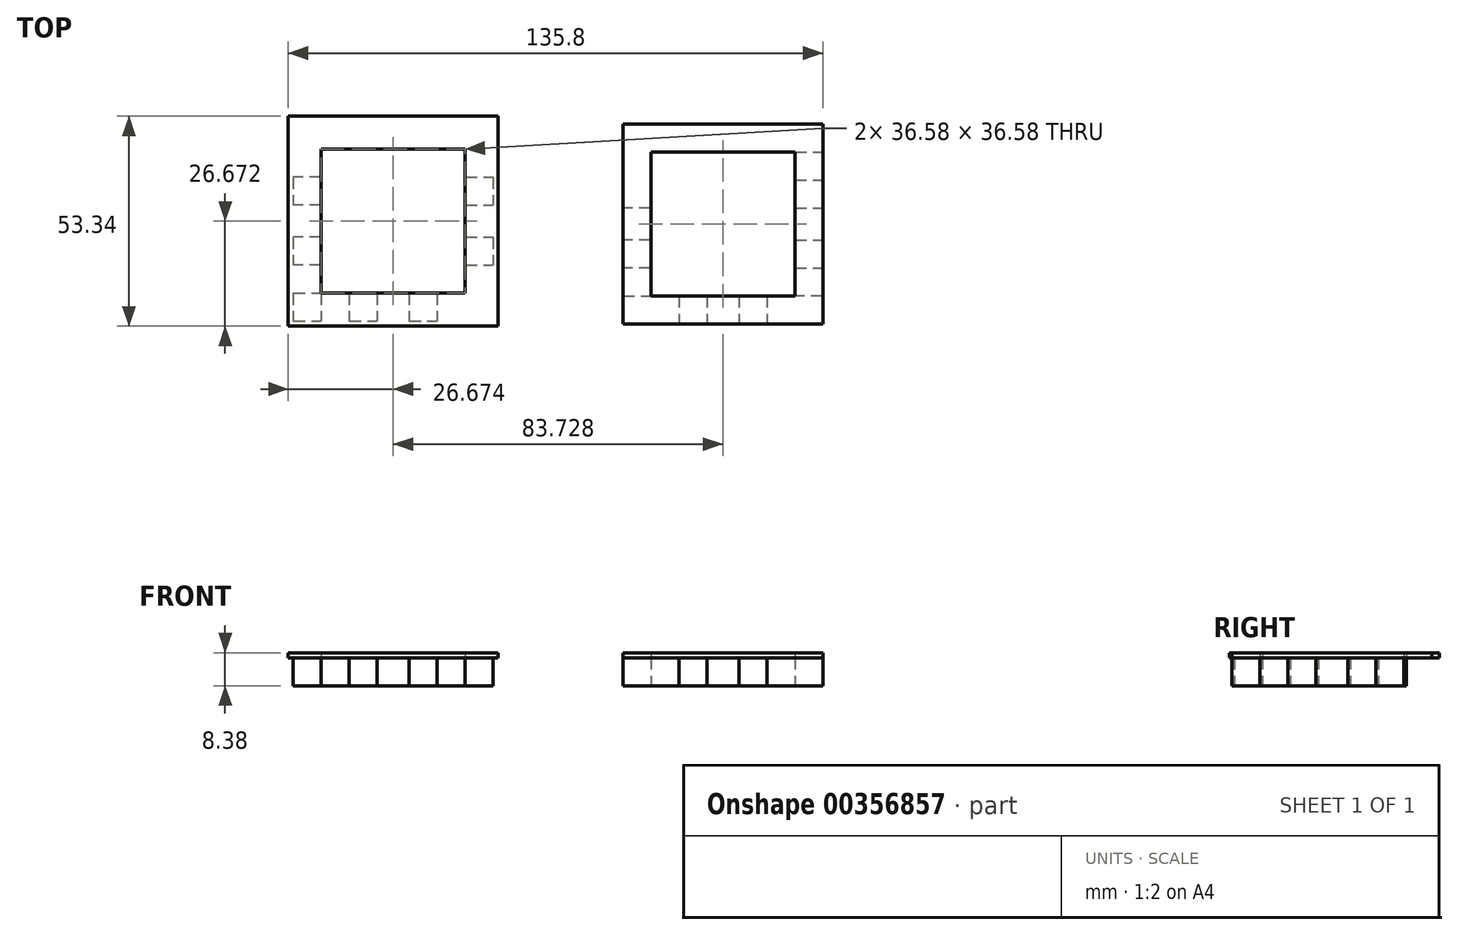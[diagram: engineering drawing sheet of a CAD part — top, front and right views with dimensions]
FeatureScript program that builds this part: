
annotation { "Feature Type Name" : "Feature", "Feature Type Description" : "" }
export const myFeature = defineFeature(function(context is Context, id is Id, definition is map)
    precondition{}
    {
        {
            var Q0;
            Q0=qCreatedBy(makeId("Top.planeOp"),FACE);
            var sketch = newSketch(context, id + "F0", { "sketchPlane" : qUnion([Q0])});
            skLineSegment(sketch, "E0.bottom", {"start": v(-28.29, 26.77) * mm, "end": v(15.4, 26.77) * mm});
            skLineSegment(sketch, "E0.top", {"start": v(-28.29, -24.03) * mm, "end": v(15.4, -24.03) * mm});
            skLineSegment(sketch, "E0.left", {"start": v(-28.29, 26.77) * mm, "end": v(-28.29, -24.03) * mm});
            skLineSegment(sketch, "E0.right", {"start": v(15.4, 26.77) * mm, "end": v(15.4, -24.03) * mm});
            skLineSegment(sketch, "E1.bottom", {"start": v(-28.29, 26.77) * mm, "end": v(-21.17, 26.77) * mm});
            skLineSegment(sketch, "E1.top", {"start": v(-28.29, 19.66) * mm, "end": v(-21.17, 19.66) * mm});
            skLineSegment(sketch, "E1.left", {"start": v(-28.29, 26.77) * mm, "end": v(-28.29, 19.66) * mm});
            skLineSegment(sketch, "E1.right", {"start": v(-21.17, 26.77) * mm, "end": v(-21.17, 19.66) * mm});
            skLineSegment(sketch, "E2.bottom", {"start": v(-21.17, 26.77) * mm, "end": v(-14.06, 26.77) * mm});
            skLineSegment(sketch, "E2.top", {"start": v(-21.17, 19.66) * mm, "end": v(-14.06, 19.66) * mm});
            skLineSegment(sketch, "E2.right", {"start": v(-14.06, 26.77) * mm, "end": v(-14.06, 19.66) * mm});
            skLineSegment(sketch, "E3.bottom", {"start": v(-14.06, 26.77) * mm, "end": v(-6.95, 26.77) * mm});
            skLineSegment(sketch, "E3.top", {"start": v(-14.06, 19.66) * mm, "end": v(-6.95, 19.66) * mm});
            skLineSegment(sketch, "E3.right", {"start": v(-6.95, 26.77) * mm, "end": v(-6.95, 19.66) * mm});
            skLineSegment(sketch, "E4.bottom", {"start": v(-6.95, 26.77) * mm, "end": v(1.18, 26.77) * mm});
            skLineSegment(sketch, "E4.top", {"start": v(-6.95, 19.66) * mm, "end": v(1.18, 19.66) * mm});
            skLineSegment(sketch, "E4.right", {"start": v(1.18, 26.77) * mm, "end": v(1.18, 19.66) * mm});
            skLineSegment(sketch, "E5.bottom", {"start": v(1.18, 26.77) * mm, "end": v(8.3, 26.77) * mm});
            skLineSegment(sketch, "E5.top", {"start": v(1.18, 19.66) * mm, "end": v(8.3, 19.66) * mm});
            skLineSegment(sketch, "E5.right", {"start": v(8.3, 26.77) * mm, "end": v(8.3, 19.66) * mm});
            skLineSegment(sketch, "E6.bottom", {"start": v(8.3, 26.77) * mm, "end": v(22.51, 26.77) * mm});
            skLineSegment(sketch, "E6.top", {"start": v(8.3, 19.66) * mm, "end": v(22.51, 19.66) * mm});
            skLineSegment(sketch, "E6.right", {"start": v(22.51, 26.77) * mm, "end": v(22.51, 19.66) * mm});
            skLineSegment(sketch, "E7.bottom", {"start": v(15.4, 26.77) * mm, "end": v(22.51, 26.77) * mm});
            skLineSegment(sketch, "E7.top", {"start": v(15.4, 19.66) * mm, "end": v(22.51, 19.66) * mm});
            skLineSegment(sketch, "E7.right", {"start": v(15.4, 26.77) * mm, "end": v(15.4, 19.66) * mm});
            skLineSegment(sketch, "E8.top", {"start": v(15.4, 12.55) * mm, "end": v(22.51, 12.55) * mm});
            skLineSegment(sketch, "E8.left", {"start": v(22.51, 19.66) * mm, "end": v(22.51, 12.55) * mm});
            skLineSegment(sketch, "E8.right", {"start": v(15.4, 19.66) * mm, "end": v(15.4, 12.55) * mm});
            skLineSegment(sketch, "E9.top", {"start": v(15.4, 5.44) * mm, "end": v(22.51, 5.44) * mm});
            skLineSegment(sketch, "E9.left", {"start": v(22.51, 12.55) * mm, "end": v(22.51, 5.44) * mm});
            skLineSegment(sketch, "E9.right", {"start": v(15.4, 12.55) * mm, "end": v(15.4, 5.44) * mm});
            skLineSegment(sketch, "E10.top", {"start": v(15.4, -2.7) * mm, "end": v(22.51, -2.7) * mm});
            skLineSegment(sketch, "E10.left", {"start": v(22.51, 5.44) * mm, "end": v(22.51, -2.7) * mm});
            skLineSegment(sketch, "E10.right", {"start": v(15.4, 5.44) * mm, "end": v(15.4, -2.7) * mm});
            skLineSegment(sketch, "E11.top", {"start": v(15.4, -9.8) * mm, "end": v(22.51, -9.8) * mm});
            skLineSegment(sketch, "E11.left", {"start": v(22.51, -2.7) * mm, "end": v(22.51, -9.8) * mm});
            skLineSegment(sketch, "E11.right", {"start": v(15.4, -2.7) * mm, "end": v(15.4, -9.8) * mm});
            skLineSegment(sketch, "E12.top", {"start": v(15.4, -16.92) * mm, "end": v(22.51, -16.92) * mm});
            skLineSegment(sketch, "E12.left", {"start": v(22.51, -9.8) * mm, "end": v(22.51, -16.92) * mm});
            skLineSegment(sketch, "E12.right", {"start": v(15.4, -9.8) * mm, "end": v(15.4, -16.92) * mm});
            skLineSegment(sketch, "E13.top", {"start": v(15.4, -24.03) * mm, "end": v(22.51, -24.03) * mm});
            skLineSegment(sketch, "E13.left", {"start": v(22.51, -16.92) * mm, "end": v(22.51, -24.03) * mm});
            skLineSegment(sketch, "E13.right", {"start": v(15.4, -16.92) * mm, "end": v(15.4, -24.03) * mm});
            skLineSegment(sketch, "E14.bottom", {"start": v(22.51, -16.92) * mm, "end": v(8.3, -16.92) * mm});
            skLineSegment(sketch, "E14.top", {"start": v(22.51, -24.03) * mm, "end": v(8.3, -24.03) * mm});
            skLineSegment(sketch, "E14.right", {"start": v(8.3, -16.92) * mm, "end": v(8.3, -24.03) * mm});
            skLineSegment(sketch, "E15.bottom", {"start": v(8.3, -16.92) * mm, "end": v(1.18, -16.92) * mm});
            skLineSegment(sketch, "E15.top", {"start": v(8.3, -24.03) * mm, "end": v(1.18, -24.03) * mm});
            skLineSegment(sketch, "E15.right", {"start": v(1.18, -16.92) * mm, "end": v(1.18, -24.03) * mm});
            skLineSegment(sketch, "E16.bottom", {"start": v(1.18, -16.92) * mm, "end": v(-6.95, -16.92) * mm});
            skLineSegment(sketch, "E16.top", {"start": v(1.18, -24.03) * mm, "end": v(-6.95, -24.03) * mm});
            skLineSegment(sketch, "E16.right", {"start": v(-6.95, -16.92) * mm, "end": v(-6.95, -24.03) * mm});
            skLineSegment(sketch, "E17.bottom", {"start": v(-6.95, -16.92) * mm, "end": v(-14.06, -16.92) * mm});
            skLineSegment(sketch, "E17.top", {"start": v(-6.95, -24.03) * mm, "end": v(-14.06, -24.03) * mm});
            skLineSegment(sketch, "E17.right", {"start": v(-14.06, -16.92) * mm, "end": v(-14.06, -24.03) * mm});
            skLineSegment(sketch, "E18.bottom", {"start": v(-21.17, 19.66) * mm, "end": v(-28.29, 19.66) * mm});
            skLineSegment(sketch, "E18.top", {"start": v(-21.17, 12.55) * mm, "end": v(-28.29, 12.55) * mm});
            skLineSegment(sketch, "E18.left", {"start": v(-21.17, 19.66) * mm, "end": v(-21.17, 12.55) * mm});
            skLineSegment(sketch, "E18.right", {"start": v(-28.29, 19.66) * mm, "end": v(-28.29, 12.55) * mm});
            skLineSegment(sketch, "E19.top", {"start": v(-21.17, 5.44) * mm, "end": v(-28.29, 5.44) * mm});
            skLineSegment(sketch, "E19.left", {"start": v(-21.17, 12.55) * mm, "end": v(-21.17, 5.44) * mm});
            skLineSegment(sketch, "E19.right", {"start": v(-28.29, 12.55) * mm, "end": v(-28.29, 5.44) * mm});
            skLineSegment(sketch, "E20.top", {"start": v(-21.17, -2.7) * mm, "end": v(-28.29, -2.7) * mm});
            skLineSegment(sketch, "E20.left", {"start": v(-21.17, 5.44) * mm, "end": v(-21.17, -2.7) * mm});
            skLineSegment(sketch, "E20.right", {"start": v(-28.29, 5.44) * mm, "end": v(-28.29, -2.7) * mm});
            skLineSegment(sketch, "E21.top", {"start": v(-21.17, -9.8) * mm, "end": v(-28.29, -9.8) * mm});
            skLineSegment(sketch, "E21.left", {"start": v(-21.17, -2.7) * mm, "end": v(-21.17, -9.8) * mm});
            skLineSegment(sketch, "E21.right", {"start": v(-28.29, -2.7) * mm, "end": v(-28.29, -9.8) * mm});
            skLineSegment(sketch, "E22.bottom", {"start": v(-28.29, -9.8) * mm, "end": v(-21.17, -9.8) * mm});
            skLineSegment(sketch, "E22.top", {"start": v(-28.29, -16.92) * mm, "end": v(-21.17, -16.92) * mm});
            skLineSegment(sketch, "E22.left", {"start": v(-28.29, -9.8) * mm, "end": v(-28.29, -16.92) * mm});
            skLineSegment(sketch, "E22.right", {"start": v(-21.17, -9.8) * mm, "end": v(-21.17, -16.92) * mm});
            skLineSegment(sketch, "E23.top", {"start": v(-28.29, -24.03) * mm, "end": v(-21.17, -24.03) * mm});
            skLineSegment(sketch, "E23.left", {"start": v(-28.29, -16.92) * mm, "end": v(-28.29, -24.03) * mm});
            skLineSegment(sketch, "E23.right", {"start": v(-21.17, -16.92) * mm, "end": v(-21.17, -24.03) * mm});
            skLineSegment(sketch, "E24.bottom", {"start": v(-21.17, -16.92) * mm, "end": v(-14.06, -16.92) * mm});
            skLineSegment(sketch, "E24.top", {"start": v(-21.17, -24.03) * mm, "end": v(-14.06, -24.03) * mm});
            skLineSegment(sketch, "E25.bottom", {"start": v(55.44, 26.09) * mm, "end": v(106.24, 26.09) * mm});
            skLineSegment(sketch, "E25.top", {"start": v(55.44, -24.71) * mm, "end": v(106.24, -24.71) * mm});
            skLineSegment(sketch, "E25.left", {"start": v(55.44, 26.09) * mm, "end": v(55.44, -24.71) * mm});
            skLineSegment(sketch, "E25.right", {"start": v(106.24, 26.09) * mm, "end": v(106.24, -24.71) * mm});
            skLineSegment(sketch, "E26.bottom", {"start": v(55.44, 26.09) * mm, "end": v(62.55, 26.09) * mm});
            skLineSegment(sketch, "E26.top", {"start": v(55.44, 18.97) * mm, "end": v(62.55, 18.97) * mm});
            skLineSegment(sketch, "E26.left", {"start": v(55.44, 26.09) * mm, "end": v(55.44, 18.97) * mm});
            skLineSegment(sketch, "E26.right", {"start": v(62.55, 26.09) * mm, "end": v(62.55, 18.97) * mm});
            skLineSegment(sketch, "E27.bottom", {"start": v(62.55, 26.09) * mm, "end": v(69.67, 26.09) * mm});
            skLineSegment(sketch, "E27.top", {"start": v(62.55, 18.97) * mm, "end": v(69.67, 18.97) * mm});
            skLineSegment(sketch, "E27.right", {"start": v(69.67, 26.09) * mm, "end": v(69.67, 18.97) * mm});
            skLineSegment(sketch, "E28.bottom", {"start": v(69.67, 26.09) * mm, "end": v(76.78, 26.09) * mm});
            skLineSegment(sketch, "E28.top", {"start": v(69.67, 18.97) * mm, "end": v(76.78, 18.97) * mm});
            skLineSegment(sketch, "E28.right", {"start": v(76.78, 26.09) * mm, "end": v(76.78, 18.97) * mm});
            skLineSegment(sketch, "E29.bottom", {"start": v(76.78, 26.09) * mm, "end": v(84.9, 26.09) * mm});
            skLineSegment(sketch, "E29.top", {"start": v(76.78, 18.97) * mm, "end": v(84.9, 18.97) * mm});
            skLineSegment(sketch, "E29.right", {"start": v(84.9, 26.09) * mm, "end": v(84.9, 18.97) * mm});
            skLineSegment(sketch, "E30.bottom", {"start": v(84.9, 26.09) * mm, "end": v(92.02, 26.09) * mm});
            skLineSegment(sketch, "E30.top", {"start": v(84.9, 18.97) * mm, "end": v(92.02, 18.97) * mm});
            skLineSegment(sketch, "E30.right", {"start": v(92.02, 26.09) * mm, "end": v(92.02, 18.97) * mm});
            skLineSegment(sketch, "E31.bottom", {"start": v(92.02, 26.09) * mm, "end": v(99.13, 26.09) * mm});
            skLineSegment(sketch, "E31.top", {"start": v(92.02, 18.97) * mm, "end": v(99.13, 18.97) * mm});
            skLineSegment(sketch, "E31.right", {"start": v(99.13, 26.09) * mm, "end": v(99.13, 18.97) * mm});
            skLineSegment(sketch, "E32.bottom", {"start": v(99.13, 26.09) * mm, "end": v(106.24, 26.09) * mm});
            skLineSegment(sketch, "E32.top", {"start": v(99.13, 18.97) * mm, "end": v(106.24, 18.97) * mm});
            skLineSegment(sketch, "E32.right", {"start": v(106.24, 26.09) * mm, "end": v(106.24, 18.97) * mm});
            skLineSegment(sketch, "E33.top", {"start": v(99.13, 11.86) * mm, "end": v(106.24, 11.86) * mm});
            skLineSegment(sketch, "E33.left", {"start": v(99.13, 18.97) * mm, "end": v(99.13, 11.86) * mm});
            skLineSegment(sketch, "E33.right", {"start": v(106.24, 18.97) * mm, "end": v(106.24, 11.86) * mm});
            skLineSegment(sketch, "E34.top", {"start": v(99.13, 4.75) * mm, "end": v(106.24, 4.75) * mm});
            skLineSegment(sketch, "E34.left", {"start": v(99.13, 11.86) * mm, "end": v(99.13, 4.75) * mm});
            skLineSegment(sketch, "E34.right", {"start": v(106.24, 11.86) * mm, "end": v(106.24, 4.75) * mm});
            skLineSegment(sketch, "E35.top", {"start": v(99.13, -3.38) * mm, "end": v(106.24, -3.38) * mm});
            skLineSegment(sketch, "E35.left", {"start": v(99.13, 4.75) * mm, "end": v(99.13, -3.38) * mm});
            skLineSegment(sketch, "E35.right", {"start": v(106.24, 4.75) * mm, "end": v(106.24, -3.38) * mm});
            skLineSegment(sketch, "E36.top", {"start": v(99.13, -10.49) * mm, "end": v(106.24, -10.49) * mm});
            skLineSegment(sketch, "E36.left", {"start": v(99.13, -3.38) * mm, "end": v(99.13, -10.49) * mm});
            skLineSegment(sketch, "E36.right", {"start": v(106.24, -3.38) * mm, "end": v(106.24, -10.49) * mm});
            skLineSegment(sketch, "E37.top", {"start": v(99.13, -17.6) * mm, "end": v(106.24, -17.6) * mm});
            skLineSegment(sketch, "E37.left", {"start": v(99.13, -10.49) * mm, "end": v(99.13, -17.6) * mm});
            skLineSegment(sketch, "E37.right", {"start": v(106.24, -10.49) * mm, "end": v(106.24, -17.6) * mm});
            skLineSegment(sketch, "E38.top", {"start": v(99.13, -24.71) * mm, "end": v(106.24, -24.71) * mm});
            skLineSegment(sketch, "E38.left", {"start": v(99.13, -17.6) * mm, "end": v(99.13, -24.71) * mm});
            skLineSegment(sketch, "E38.right", {"start": v(106.24, -17.6) * mm, "end": v(106.24, -24.71) * mm});
            skLineSegment(sketch, "E39.bottom", {"start": v(99.13, -17.6) * mm, "end": v(92.02, -17.6) * mm});
            skLineSegment(sketch, "E39.top", {"start": v(99.13, -24.71) * mm, "end": v(92.02, -24.71) * mm});
            skLineSegment(sketch, "E39.right", {"start": v(92.02, -17.6) * mm, "end": v(92.02, -24.71) * mm});
            skLineSegment(sketch, "E40.bottom", {"start": v(92.02, -17.6) * mm, "end": v(84.9, -17.6) * mm});
            skLineSegment(sketch, "E40.top", {"start": v(92.02, -24.71) * mm, "end": v(84.9, -24.71) * mm});
            skLineSegment(sketch, "E40.right", {"start": v(84.9, -17.6) * mm, "end": v(84.9, -24.71) * mm});
            skLineSegment(sketch, "E41.bottom", {"start": v(84.9, -17.6) * mm, "end": v(76.78, -17.6) * mm});
            skLineSegment(sketch, "E41.top", {"start": v(84.9, -24.71) * mm, "end": v(76.78, -24.71) * mm});
            skLineSegment(sketch, "E41.right", {"start": v(76.78, -17.6) * mm, "end": v(76.78, -24.71) * mm});
            skLineSegment(sketch, "E42.bottom", {"start": v(76.78, -17.6) * mm, "end": v(69.67, -17.6) * mm});
            skLineSegment(sketch, "E42.top", {"start": v(76.78, -24.71) * mm, "end": v(69.67, -24.71) * mm});
            skLineSegment(sketch, "E42.right", {"start": v(69.67, -17.6) * mm, "end": v(69.67, -24.71) * mm});
            skLineSegment(sketch, "E43.bottom", {"start": v(62.55, 18.97) * mm, "end": v(55.44, 18.97) * mm});
            skLineSegment(sketch, "E43.top", {"start": v(62.55, 11.86) * mm, "end": v(55.44, 11.86) * mm});
            skLineSegment(sketch, "E43.left", {"start": v(62.55, 18.97) * mm, "end": v(62.55, 11.86) * mm});
            skLineSegment(sketch, "E43.right", {"start": v(55.44, 18.97) * mm, "end": v(55.44, 11.86) * mm});
            skLineSegment(sketch, "E44.top", {"start": v(62.55, 4.75) * mm, "end": v(55.44, 4.75) * mm});
            skLineSegment(sketch, "E44.left", {"start": v(62.55, 11.86) * mm, "end": v(62.55, 4.75) * mm});
            skLineSegment(sketch, "E44.right", {"start": v(55.44, 11.86) * mm, "end": v(55.44, 4.75) * mm});
            skLineSegment(sketch, "E45.top", {"start": v(62.55, -3.38) * mm, "end": v(55.44, -3.38) * mm});
            skLineSegment(sketch, "E45.left", {"start": v(62.55, 4.75) * mm, "end": v(62.55, -3.38) * mm});
            skLineSegment(sketch, "E45.right", {"start": v(55.44, 4.75) * mm, "end": v(55.44, -3.38) * mm});
            skLineSegment(sketch, "E46.top", {"start": v(62.55, -10.49) * mm, "end": v(55.44, -10.49) * mm});
            skLineSegment(sketch, "E46.left", {"start": v(62.55, -3.38) * mm, "end": v(62.55, -10.49) * mm});
            skLineSegment(sketch, "E46.right", {"start": v(55.44, -3.38) * mm, "end": v(55.44, -10.49) * mm});
            skLineSegment(sketch, "E47.top", {"start": v(62.55, -17.6) * mm, "end": v(55.44, -17.6) * mm});
            skLineSegment(sketch, "E47.left", {"start": v(62.55, -10.49) * mm, "end": v(62.55, -17.6) * mm});
            skLineSegment(sketch, "E47.right", {"start": v(55.44, -10.49) * mm, "end": v(55.44, -17.6) * mm});
            skLineSegment(sketch, "E48.bottom", {"start": v(62.55, -17.6) * mm, "end": v(69.67, -17.6) * mm});
            skLineSegment(sketch, "E48.top", {"start": v(62.55, -24.71) * mm, "end": v(69.67, -24.71) * mm});
            skLineSegment(sketch, "E48.left", {"start": v(62.55, -17.6) * mm, "end": v(62.55, -24.71) * mm});
            skLineSegment(sketch, "E49.top", {"start": v(62.55, -24.71) * mm, "end": v(55.44, -24.71) * mm});
            skLineSegment(sketch, "E49.right", {"start": v(55.44, -17.6) * mm, "end": v(55.44, -24.71) * mm});
            skSolve(sketch);
        }
        {
            var Q0;
            Q0=makeQuery(id+"F0.imprint","IMPRINT",FACE,{"disambiguationData":[TD([[makeQuery(id+"F0.imprint","IMPRINT",EDGE,{"derivedFrom":sQuery(id+"F0.wireOp",EDGE,"E1.bottom")}),-1.0]])]});
            var Q1;
            Q1=makeQuery(id+"F0.imprint","IMPRINT",FACE,{"disambiguationData":[TD([[makeQuery(id+"F0.imprint","IMPRINT",EDGE,{"derivedFrom":sQuery(id+"F0.wireOp",EDGE,"E3.bottom")}),-1.0]])]});
            var Q2;
            Q2=makeQuery(id+"F0.imprint","IMPRINT",FACE,{"disambiguationData":[TD([[makeQuery(id+"F0.imprint","IMPRINT",EDGE,{"derivedFrom":sQuery(id+"F0.wireOp",EDGE,"E5.bottom")}),-1.0]])]});
            var Q3;
            Q3=makeQuery(id+"F0.imprint","IMPRINT",FACE,{"disambiguationData":[TD([[makeQuery(id+"F0.imprint","IMPRINT",EDGE,{"derivedFrom":sQuery(id+"F0.wireOp",EDGE,"E7.bottom")}),-1.0]])]});
            var Q4;
            Q4=makeQuery(id+"F0.imprint","IMPRINT",FACE,{"disambiguationData":[TD([[makeQuery(id+"F0.imprint","IMPRINT",EDGE,{"derivedFrom":sQuery(id+"F0.wireOp",EDGE,"E8.top")}),-1.0]])]});
            var Q5;
            Q5=makeQuery(id+"F0.imprint","IMPRINT",FACE,{"disambiguationData":[TD([[makeQuery(id+"F0.imprint","IMPRINT",EDGE,{"derivedFrom":sQuery(id+"F0.wireOp",EDGE,"E10.top")}),-1.0]])]});
            var Q6;
            {var subQ0=sQuery(id+"F0.wireOp",EDGE,"E13.right");Q6=makeQuery(id+"F0.imprint","IMPRINT",FACE,{"disambiguationData":[TD([[makeQuery(id+"F0.imprint","IMPRINT",EDGE,{"derivedFrom":subQ0}),1.0]])]});}
            var Q7;
            Q7=makeQuery(id+"F0.imprint","IMPRINT",FACE,{"disambiguationData":[TD([[makeQuery(id+"F0.imprint","IMPRINT",EDGE,{"derivedFrom":sQuery(id+"F0.wireOp",EDGE,"E15.bottom")}),1.0]])]});
            var Q8;
            Q8=makeQuery(id+"F0.imprint","IMPRINT",FACE,{"disambiguationData":[TD([[makeQuery(id+"F0.imprint","IMPRINT",EDGE,{"derivedFrom":sQuery(id+"F0.wireOp",EDGE,"E2.top")}),-1.0]])]});
            var Q9;
            Q9=makeQuery(id+"F0.imprint","IMPRINT",FACE,{"disambiguationData":[TD([[makeQuery(id+"F0.imprint","IMPRINT",EDGE,{"derivedFrom":sQuery(id+"F0.wireOp",EDGE,"E17.bottom")}),1.0]])]});
            var Q10;
            Q10=makeQuery(id+"F0.imprint","IMPRINT",FACE,{"disambiguationData":[TD([[makeQuery(id+"F0.imprint","IMPRINT",EDGE,{"derivedFrom":sQuery(id+"F0.wireOp",EDGE,"E22.top")}),-1.0]])]});
            var Q11;
            Q11=makeQuery(id+"F0.imprint","IMPRINT",FACE,{"disambiguationData":[TD([[makeQuery(id+"F0.imprint","IMPRINT",EDGE,{"derivedFrom":sQuery(id+"F0.wireOp",EDGE,"E20.top")}),1.0]])]});
            var Q12;
            Q12=makeQuery(id+"F0.imprint","IMPRINT",FACE,{"disambiguationData":[TD([[makeQuery(id+"F0.imprint","IMPRINT",EDGE,{"derivedFrom":sQuery(id+"F0.wireOp",EDGE,"E18.top")}),1.0]])]});
            var Q13;
            Q13=makeQuery(id+"F0.imprint","IMPRINT",FACE,{"disambiguationData":[TD([[makeQuery(id+"F0.imprint","IMPRINT",EDGE,{"derivedFrom":sQuery(id+"F0.wireOp",EDGE,"E27.top")}),-1.0]])]});
            var Q14;
            Q14=makeQuery(id+"F0.imprint","IMPRINT",FACE,{"disambiguationData":[TD([[makeQuery(id+"F0.imprint","IMPRINT",EDGE,{"derivedFrom":sQuery(id+"F0.wireOp",EDGE,"E31.bottom")}),-1.0]])]});
            var Q15;
            Q15=makeQuery(id+"F0.imprint","IMPRINT",FACE,{"disambiguationData":[TD([[makeQuery(id+"F0.imprint","IMPRINT",EDGE,{"derivedFrom":sQuery(id+"F0.wireOp",EDGE,"E29.bottom")}),-1.0]])]});
            var Q16;
            Q16=makeQuery(id+"F0.imprint","IMPRINT",FACE,{"disambiguationData":[TD([[makeQuery(id+"F0.imprint","IMPRINT",EDGE,{"derivedFrom":sQuery(id+"F0.wireOp",EDGE,"E43.bottom")}),1.0]])]});
            var Q17;
            Q17=makeQuery(id+"F0.imprint","IMPRINT",FACE,{"disambiguationData":[TD([[makeQuery(id+"F0.imprint","IMPRINT",EDGE,{"derivedFrom":sQuery(id+"F0.wireOp",EDGE,"E44.top")}),1.0]])]});
            var Q18;
            Q18=makeQuery(id+"F0.imprint","IMPRINT",FACE,{"disambiguationData":[TD([[makeQuery(id+"F0.imprint","IMPRINT",EDGE,{"derivedFrom":sQuery(id+"F0.wireOp",EDGE,"E36.top")}),-1.0]])]});
            var Q19;
            Q19=makeQuery(id+"F0.imprint","IMPRINT",FACE,{"disambiguationData":[TD([[makeQuery(id+"F0.imprint","IMPRINT",EDGE,{"derivedFrom":sQuery(id+"F0.wireOp",EDGE,"E34.top")}),-1.0]])]});
            var Q20;
            Q20=makeQuery(id+"F0.imprint","IMPRINT",FACE,{"disambiguationData":[TD([[makeQuery(id+"F0.imprint","IMPRINT",EDGE,{"derivedFrom":sQuery(id+"F0.wireOp",EDGE,"E46.top")}),1.0]])]});
            var Q21;
            Q21=makeQuery(id+"F0.imprint","IMPRINT",FACE,{"disambiguationData":[TD([[makeQuery(id+"F0.imprint","IMPRINT",EDGE,{"derivedFrom":sQuery(id+"F0.wireOp",EDGE,"E32.top")}),-1.0]])]});
            var Q22;
            Q22=makeQuery(id+"F0.imprint","IMPRINT",FACE,{"disambiguationData":[TD([[makeQuery(id+"F0.imprint","IMPRINT",EDGE,{"derivedFrom":sQuery(id+"F0.wireOp",EDGE,"E27.bottom")}),-1.0]])]});
            var Q23;
            Q23=makeQuery(id+"F0.imprint","IMPRINT",FACE,{"disambiguationData":[TD([[makeQuery(id+"F0.imprint","IMPRINT",EDGE,{"derivedFrom":sQuery(id+"F0.wireOp",EDGE,"E42.bottom")}),1.0]])]});
            var Q24;
            Q24=makeQuery(id+"F0.imprint","IMPRINT",FACE,{"disambiguationData":[TD([[makeQuery(id+"F0.imprint","IMPRINT",EDGE,{"derivedFrom":sQuery(id+"F0.wireOp",EDGE,"E40.bottom")}),1.0]])]});
            extrude(context, id + "F1", {"entities" : qUnion([Q0, Q1, Q2, Q3, Q4, Q5, Q6, Q7, Q8, Q9, Q10, Q11, Q12, Q13, Q14, Q15, Q16, Q17, Q18, Q19, Q20, Q21, Q22, Q23, Q24]), "depth" : 7.11 * mm});
        }
        {
            var Q0;
            Q0=makeQuery(id+"F1.opExtrude","CAP_FACE",FACE,{"disambiguationData":[OSD([sQuery(id+"F0.wireOp",EDGE,"E2.top"),sQuery(id+"F0.wireOp",EDGE,"E3.bottom"),sQuery(id+"F0.wireOp",EDGE,"E2.right"),sQuery(id+"F0.wireOp",EDGE,"E4.top"),sQuery(id+"F0.wireOp",EDGE,"E3.right"),sQuery(id+"F0.wireOp",EDGE,"E5.bottom"),sQuery(id+"F0.wireOp",EDGE,"E4.right"),sQuery(id+"F0.wireOp",EDGE,"E6.top"),sQuery(id+"F0.wireOp",EDGE,"E5.right"),sQuery(id+"F0.wireOp",EDGE,"E8.right"),sQuery(id+"F0.wireOp",EDGE,"E8.top"),sQuery(id+"F0.wireOp",EDGE,"E9.left"),sQuery(id+"F0.wireOp",EDGE,"E9.top"),sQuery(id+"F0.wireOp",EDGE,"E10.right"),sQuery(id+"F0.wireOp",EDGE,"E10.top"),sQuery(id+"F0.wireOp",EDGE,"E11.left"),sQuery(id+"F0.wireOp",EDGE,"E11.top"),sQuery(id+"F0.wireOp",EDGE,"E12.right"),sQuery(id+"F0.wireOp",EDGE,"E14.bottom"),sQuery(id+"F0.wireOp",EDGE,"E15.top"),sQuery(id+"F0.wireOp",EDGE,"E14.right"),sQuery(id+"F0.wireOp",EDGE,"E16.bottom"),sQuery(id+"F0.wireOp",EDGE,"E15.right"),sQuery(id+"F0.wireOp",EDGE,"E17.top"),sQuery(id+"F0.wireOp",EDGE,"E16.right"),sQuery(id+"F0.wireOp",EDGE,"E18.left"),sQuery(id+"F0.wireOp",EDGE,"E18.top"),sQuery(id+"F0.wireOp",EDGE,"E19.right"),sQuery(id+"F0.wireOp",EDGE,"E19.top"),sQuery(id+"F0.wireOp",EDGE,"E20.left"),sQuery(id+"F0.wireOp",EDGE,"E20.top"),sQuery(id+"F0.wireOp",EDGE,"E21.right"),sQuery(id+"F0.wireOp",EDGE,"E22.bottom"),sQuery(id+"F0.wireOp",EDGE,"E22.right"),sQuery(id+"F0.wireOp",EDGE,"E24.bottom"),sQuery(id+"F0.wireOp",EDGE,"E17.right")])],"isStart":false});
            var sketch = newSketch(context, id + "F2", { "sketchPlane" : qUnion([Q0])});
            skLineSegment(sketch, "E50.bottom", {"start": v(-29.56, -25.3) * mm, "end": v(23.78, -25.3) * mm});
            skLineSegment(sketch, "E50.top", {"start": v(-29.56, -16.92) * mm, "end": v(23.78, -16.92) * mm});
            skLineSegment(sketch, "E50.left", {"start": v(-29.56, -25.3) * mm, "end": v(-29.56, -16.92) * mm});
            skLineSegment(sketch, "E50.right", {"start": v(23.78, -25.3) * mm, "end": v(23.78, -16.92) * mm});
            skLineSegment(sketch, "E51.bottom", {"start": v(-29.56, -25.3) * mm, "end": v(-21.17, -25.3) * mm});
            skLineSegment(sketch, "E51.top", {"start": v(-29.56, 28.04) * mm, "end": v(-21.17, 28.04) * mm});
            skLineSegment(sketch, "E51.left", {"start": v(-29.56, -25.3) * mm, "end": v(-29.56, 28.04) * mm});
            skLineSegment(sketch, "E51.right", {"start": v(-21.17, -25.3) * mm, "end": v(-21.17, 28.04) * mm});
            skLineSegment(sketch, "E52.bottom", {"start": v(-29.56, 19.66) * mm, "end": v(23.78, 19.66) * mm});
            skLineSegment(sketch, "E52.top", {"start": v(-29.56, 28.04) * mm, "end": v(23.78, 28.04) * mm});
            skLineSegment(sketch, "E52.left", {"start": v(-29.56, 19.66) * mm, "end": v(-29.56, 28.04) * mm});
            skLineSegment(sketch, "E52.right", {"start": v(23.78, 19.66) * mm, "end": v(23.78, 28.04) * mm});
            skLineSegment(sketch, "E53.bottom", {"start": v(23.78, 28.04) * mm, "end": v(15.4, 28.04) * mm});
            skLineSegment(sketch, "E53.top", {"start": v(23.78, -25.3) * mm, "end": v(15.4, -25.3) * mm});
            skLineSegment(sketch, "E53.left", {"start": v(23.78, 28.04) * mm, "end": v(23.78, -25.3) * mm});
            skLineSegment(sketch, "E53.right", {"start": v(15.4, 28.04) * mm, "end": v(15.4, -25.3) * mm});
            skSolve(sketch);
        }
        {
            var Q0;
            Q0 = qSketchRegion(id + "F2", true);
            extrude(context, id + "F3", {"entities" : qUnion([Q0]), "depth" : 1.27 * mm});
        }
        {
            var Q0;
            Q0=makeQuery(id+"F1.opExtrude","CAP_FACE",FACE,{"disambiguationData":[OSD([sQuery(id+"F0.wireOp",EDGE,"E27.bottom"),sQuery(id+"F0.wireOp",EDGE,"E26.right"),sQuery(id+"F0.wireOp",EDGE,"E28.top"),sQuery(id+"F0.wireOp",EDGE,"E27.right"),sQuery(id+"F0.wireOp",EDGE,"E29.bottom"),sQuery(id+"F0.wireOp",EDGE,"E28.right"),sQuery(id+"F0.wireOp",EDGE,"E30.top"),sQuery(id+"F0.wireOp",EDGE,"E29.right"),sQuery(id+"F0.wireOp",EDGE,"E31.bottom"),sQuery(id+"F0.wireOp",EDGE,"E30.right"),sQuery(id+"F0.wireOp",EDGE,"E31.right"),sQuery(id+"F0.wireOp",EDGE,"E32.top"),sQuery(id+"F0.wireOp",EDGE,"E33.right"),sQuery(id+"F0.wireOp",EDGE,"E33.top"),sQuery(id+"F0.wireOp",EDGE,"E34.left"),sQuery(id+"F0.wireOp",EDGE,"E34.top"),sQuery(id+"F0.wireOp",EDGE,"E35.right"),sQuery(id+"F0.wireOp",EDGE,"E35.top"),sQuery(id+"F0.wireOp",EDGE,"E36.left"),sQuery(id+"F0.wireOp",EDGE,"E36.top"),sQuery(id+"F0.wireOp",EDGE,"E37.right"),sQuery(id+"F0.wireOp",EDGE,"E37.top"),sQuery(id+"F0.wireOp",EDGE,"E39.bottom"),sQuery(id+"F0.wireOp",EDGE,"E40.top"),sQuery(id+"F0.wireOp",EDGE,"E39.right"),sQuery(id+"F0.wireOp",EDGE,"E41.bottom"),sQuery(id+"F0.wireOp",EDGE,"E40.right"),sQuery(id+"F0.wireOp",EDGE,"E42.top"),sQuery(id+"F0.wireOp",EDGE,"E41.right"),sQuery(id+"F0.wireOp",EDGE,"E43.bottom"),sQuery(id+"F0.wireOp",EDGE,"E43.right"),sQuery(id+"F0.wireOp",EDGE,"E43.top"),sQuery(id+"F0.wireOp",EDGE,"E44.left"),sQuery(id+"F0.wireOp",EDGE,"E44.top"),sQuery(id+"F0.wireOp",EDGE,"E45.right"),sQuery(id+"F0.wireOp",EDGE,"E45.top"),sQuery(id+"F0.wireOp",EDGE,"E46.left"),sQuery(id+"F0.wireOp",EDGE,"E46.top"),sQuery(id+"F0.wireOp",EDGE,"E47.right"),sQuery(id+"F0.wireOp",EDGE,"E48.bottom"),sQuery(id+"F0.wireOp",EDGE,"E42.right"),sQuery(id+"F0.wireOp",EDGE,"E47.top")])],"isStart":false});
            var sketch = newSketch(context, id + "F4", { "sketchPlane" : qUnion([Q0])});
            skLineSegment(sketch, "E54.bottom", {"start": v(55.44, -24.71) * mm, "end": v(62.55, -24.71) * mm});
            skLineSegment(sketch, "E54.top", {"start": v(55.44, 26.09) * mm, "end": v(62.55, 26.09) * mm});
            skLineSegment(sketch, "E54.left", {"start": v(55.44, -24.71) * mm, "end": v(55.44, 26.09) * mm});
            skLineSegment(sketch, "E54.right", {"start": v(62.55, -24.71) * mm, "end": v(62.55, 26.09) * mm});
            skLineSegment(sketch, "E55.bottom", {"start": v(55.44, -24.71) * mm, "end": v(106.24, -24.71) * mm});
            skLineSegment(sketch, "E55.top", {"start": v(55.44, -17.6) * mm, "end": v(106.24, -17.6) * mm});
            skLineSegment(sketch, "E55.left", {"start": v(55.44, -24.71) * mm, "end": v(55.44, -17.6) * mm});
            skLineSegment(sketch, "E55.right", {"start": v(106.24, -24.71) * mm, "end": v(106.24, -17.6) * mm});
            skLineSegment(sketch, "E56.bottom", {"start": v(106.24, -24.71) * mm, "end": v(99.13, -24.71) * mm});
            skLineSegment(sketch, "E56.top", {"start": v(106.24, 26.09) * mm, "end": v(99.13, 26.09) * mm});
            skLineSegment(sketch, "E56.left", {"start": v(106.24, -24.71) * mm, "end": v(106.24, 26.09) * mm});
            skLineSegment(sketch, "E56.right", {"start": v(99.13, -24.71) * mm, "end": v(99.13, 26.09) * mm});
            skLineSegment(sketch, "E57.bottom", {"start": v(106.24, 26.09) * mm, "end": v(55.44, 26.09) * mm});
            skLineSegment(sketch, "E57.top", {"start": v(106.24, 18.97) * mm, "end": v(55.44, 18.97) * mm});
            skLineSegment(sketch, "E57.left", {"start": v(106.24, 26.09) * mm, "end": v(106.24, 18.97) * mm});
            skLineSegment(sketch, "E57.right", {"start": v(55.44, 26.09) * mm, "end": v(55.44, 18.97) * mm});
            skSolve(sketch);
        }
        {
            var Q0;
            Q0 = qSketchRegion(id + "F4", true);
            extrude(context, id + "F5", {"entities" : qUnion([Q0]), "depth" : 1.27 * mm});
        }
    });
